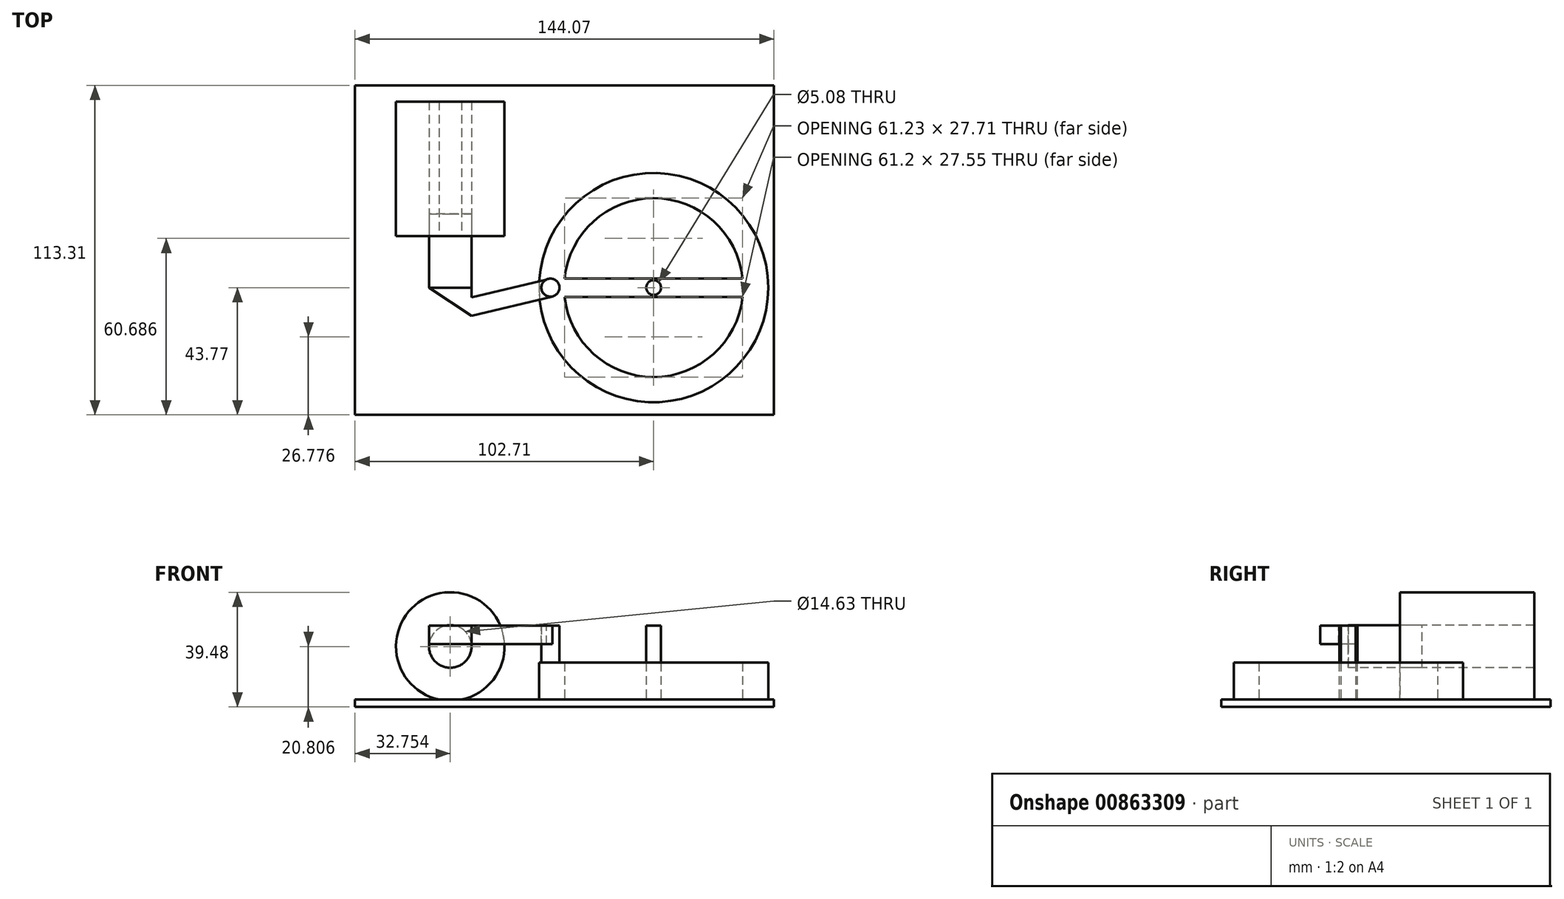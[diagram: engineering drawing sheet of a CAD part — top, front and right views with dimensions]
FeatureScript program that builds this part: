
annotation { "Feature Type Name" : "Feature", "Feature Type Description" : "" }
export const myFeature = defineFeature(function(context is Context, id is Id, definition is map)
    precondition{}
    {
        {
            var Q0;
            Q0=qCreatedBy(makeId("Top.planeOp"),FACE);
            var sketch = newSketch(context, id + "F0", { "sketchPlane" : qUnion([Q0])});
            skCircle(sketch, "E0", {"center": v(0, 0) * mm, "radius": 39.43 * mm});
            skArc(sketch, "E1", {"start": v(30.62, 3.06) * mm, "mid": v(0, 30.77) * mm, "end": v(-30.62, 3.06) * mm});
            skLineSegment(sketch, "E2", {"start": v(-30.62, 3.06) * mm, "end": v(30.62, 3.06) * mm});
            skLineSegment(sketch, "E3", {"start": v(30.6, -3.22) * mm, "end": v(-30.6, -3.22) * mm});
            skArc(sketch, "E4.trimOffspring", {"start": v(-30.6, -3.22) * mm, "mid": v(0, -30.77) * mm, "end": v(30.6, -3.22) * mm});
            skCircle(sketch, "E5", {"center": v(-35.5, 0) * mm, "radius": 3.11 * mm});
            skCircle(sketch, "E6", {"center": v(0, 0) * mm, "radius": 2.54 * mm});
            skSolve(sketch);
        }
        {
            var Q0;
            Q0 = qSketchRegion(id + "F0", true);
            extrude(context, id + "F1", {"entities" : qUnion([Q0]), "depth" : 12.7 * mm, "offsetDistance" : 25.4 * mm});
        }
        {
            var Q0;
            Q0=makeQuery(id+"F0.imprint","IMPRINT",FACE,{"disambiguationData":[TD([[makeQuery(id+"F0.imprint","IMPRINT",EDGE,{"derivedFrom":sQuery(id+"F0.wireOp",EDGE,"E5")}),1.0]])]});
            extrude(context, id + "F2", {"entities" : qUnion([Q0]), "operationType" : NewBodyOperationType.ADD, "depth" : 25.4 * mm, "offsetDistance" : 25.4 * mm});
        }
        {
            var Q0;
            Q0=qCreatedBy(makeId("Top.planeOp"),FACE);
            var sketch = newSketch(context, id + "F3", { "sketchPlane" : qUnion([Q0])});
            skCircle(sketch, "E7", {"center": v(0, 0) * mm, "radius": 2.54 * mm});
            skLineSegment(sketch, "E8.bottom", {"start": v(-102.71, 69.54) * mm, "end": v(41.36, 69.54) * mm});
            skLineSegment(sketch, "E8.top", {"start": v(-102.71, -43.77) * mm, "end": v(41.36, -43.77) * mm});
            skLineSegment(sketch, "E8.left", {"start": v(-102.71, 69.54) * mm, "end": v(-102.71, -43.77) * mm});
            skLineSegment(sketch, "E8.right", {"start": v(41.36, 69.54) * mm, "end": v(41.36, -43.77) * mm});
            skSolve(sketch);
        }
        {
            var Q0;
            Q0=makeQuery(id+"F3.imprint","IMPRINT",FACE,{"disambiguationData":[TD([[makeQuery(id+"F3.imprint","IMPRINT",EDGE,{"derivedFrom":sQuery(id+"F3.wireOp",EDGE,"E7")}),-1.0]])]});
            var Q1;
            Q1=makeQuery(id+"F3.imprint","IMPRINT",FACE,{"disambiguationData":[TD([[makeQuery(id+"F3.imprint","IMPRINT",EDGE,{"derivedFrom":sQuery(id+"F3.wireOp",EDGE,"E7")}),1.0]])]});
            extrude(context, id + "F4", {"entities" : qUnion([Q0, Q1]), "oppositeDirection" : true, "depth" : 2.54 * mm, "offsetDistance" : 25.4 * mm});
        }
        {
            var Q0;
            Q0=makeQuery(id+"F3.imprint","IMPRINT",FACE,{"disambiguationData":[TD([[makeQuery(id+"F3.imprint","IMPRINT",EDGE,{"derivedFrom":sQuery(id+"F3.wireOp",EDGE,"E7")}),1.0]])]});
            extrude(context, id + "F5", {"entities" : qUnion([Q0]), "operationType" : NewBodyOperationType.ADD, "depth" : 25.4 * mm, "offsetDistance" : 25.4 * mm});
        }
        {
            var Q0;
            Q0=qCreatedBy(makeId("Front.planeOp"),FACE);
            var sketch = newSketch(context, id + "F6", { "sketchPlane" : qUnion([Q0])});
            skCircle(sketch, "E9", {"center": v(-69.96, 18.27) * mm, "radius": 7.32 * mm});
            skCircle(sketch, "E10", {"center": v(-69.96, 18.27) * mm, "radius": 18.67 * mm});
            skSolve(sketch);
        }
        {
            var Q0;
            Q0=makeQuery(id+"F6.imprint","IMPRINT",FACE,{"disambiguationData":[TD([[makeQuery(id+"F6.imprint","IMPRINT",EDGE,{"derivedFrom":sQuery(id+"F6.wireOp",EDGE,"E9")}),-1.0]])]});
            extrude(context, id + "F7", {"entities" : qUnion([Q0]), "operationType" : NewBodyOperationType.ADD, "oppositeDirection" : true, "depth" : 64 * mm, "offsetDistance" : 25.4 * mm, "hasSecondDirection" : true, "secondDirectionOppositeDirection" : true, "secondDirectionDepth" : 17.78 * mm});
        }
        {
            var Q0;
            Q0=makeQuery(id+"F6.imprint","IMPRINT",FACE,{"disambiguationData":[TD([[makeQuery(id+"F6.imprint","IMPRINT",EDGE,{"derivedFrom":sQuery(id+"F6.wireOp",EDGE,"E9")}),1.0]])]});
            extrude(context, id + "F8", {"entities" : qUnion([Q0]), "oppositeDirection" : true, "depth" : 25.4 * mm, "offsetDistance" : 25.4 * mm});
        }
        {
            var Q0;
            Q0=makeQuery(id+"F2.opExtrude","CAP_FACE",FACE,{"disambiguationData":[OSD([sQuery(id+"F0.wireOp",EDGE,"E5")])],"isStart":false});
            var sketch = newSketch(context, id + "F9", { "sketchPlane" : qUnion([Q0])});
            skLineSegment(sketch, "E11", {"start": v(-35.56, 3.1) * mm, "end": v(-62.62, -3.36) * mm});
            skLineSegment(sketch, "E12", {"start": v(-62.62, -3.36) * mm, "end": v(-62.62, -9.68) * mm});
            skLineSegment(sketch, "E13", {"start": v(-62.62, -9.68) * mm, "end": v(-34.78, -3.02) * mm});
            skCircle(sketch, "E14", {"center": v(-35.5, 0) * mm, "radius": 3.11 * mm});
            skLineSegment(sketch, "E15", {"start": v(-62.62, -9.68) * mm, "end": v(-77.22, 0) * mm});
            skLineSegment(sketch, "E16", {"start": v(-77.22, 0) * mm, "end": v(-62.62, 0) * mm});
            skLineSegment(sketch, "E17", {"start": v(-62.62, 0) * mm, "end": v(-62.62, -3.36) * mm});
            skSolve(sketch);
        }
        {
            var Q0;
            {var subQ0=sQuery(id+"F9.wireOp",EDGE,"E12");Q0=makeQuery(id+"F9.imprint","IMPRINT",FACE,{"disambiguationData":[TD([[makeQuery(id+"F9.imprint","IMPRINT",EDGE,{"derivedFrom":subQ0}),1.0]])]});}
            var Q1;
            Q1=makeQuery(id+"F9.imprint","IMPRINT",FACE,{"disambiguationData":[TD([[makeQuery(id+"F9.imprint","IMPRINT",EDGE,{"derivedFrom":sQuery(id+"F9.wireOp",EDGE,"E12")}),-1.0]])]});
            extrude(context, id + "F10", {"entities" : qUnion([Q0, Q1]), "operationType" : NewBodyOperationType.ADD, "oppositeDirection" : true, "depth" : 6.35 * mm, "offsetDistance" : 25.4 * mm});
        }
    });
